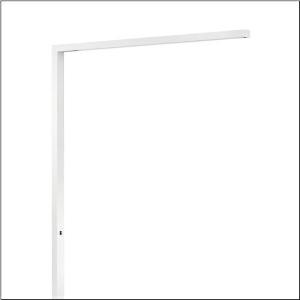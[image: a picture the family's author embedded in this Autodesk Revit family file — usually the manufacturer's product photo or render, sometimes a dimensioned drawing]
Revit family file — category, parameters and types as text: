
# Revit family: silica_r__11_floor_5mx51bs3wzk00002xx_06fb
name_source: partatom
category: Lighting Fixtures
units: mm (PartAtom-declared; Revit-internal decimal feet)

## family parameters
Cut with Voids When Loaded = No
Host = Face
Light Source = No
Part Type = Normal
Room Calculation Point = No
Round Connector Dimension = Use Diameter
Shared = No

## types (1)
- --- (1 x LED, 3960 lm / 8500 lm, 24.4 W / 54.9 W, 4000K)
    Apparent Load = 79 VA
    CIE Flux Codes = 82 97 100 100 100 / - - - 0 100
    Color Rendering = 80
    Color Temperature = 4000K
    Default Elevation = 1800 mm
    Description = Silica® 11 Floor, floorstanding luminaire, of PMMA, primary optical cover: cover panel, of PMMA, light emission: indirect/direct distribution, primary light characteristic: symmetric, installation type: not mounted, LED, rated luminous flux: 12.460lm, luminous efficacy: 157lm/W, light colour: 840, colour temperature: 4000K, daylight-dependent control, mains connection: 230V, AC, 50Hz, connection cable pre-assembled, cable length: 3m, rated input power: 79W, luminaire head, rectangular, rounded, of aluminium, coated, traffic white (RAL 9016), supporting column, angular, of aluminium, coated, traffic white (RAL 9016), baseplate, of steel, coated, traffic white (RAL 9016), length: 1.316mm, width: 65mm, protection rating (complete): IP20, insulation class (complete): insulation class I (protective earthing), certification: CE, permissible operating ambient temperature: 0..+35°C, standard: EN 50419, packaging unit: 1 piece
    Height = 40 mm  [stored 0.131234 ft]
    Lamp = 1 x LED
    Lamp Light Flux = 3960 lm / 8500 lm
    Lamp Power = 24.4 W / 54.9 W
    Lamp count = 1
    Length = 1317 mm
    Luminous efficacy = 157 lm/W
    Manufacturer = Siteco
    ModVariant = No
    Model = 5MX51BS3WZK00002XX
    Mounting Place = Floor
    Mounting Type = Freestanding
    Number of Poles = 1
    OnlyDefault = Yes
    Power Factor = 1
    Product Name = Silica® 11 Floor
    Product group = floorstanding luminaire
    ProductGroupID = 1301
    Protection Class = Protection class I
    Protection Degree = IP 20
    RLX_Detail_Level = 1
    RLX_Emergency_Light_Flux = 0 lm
    RLX_Emergency_Type = 0
    RLX_Emergency_Type_DB = No
    RlxData = <blob elided: 18153 chars, md5=e39972d7>
    Socket = socket
    Standby Power = 0 W
    System Light Flux = 12460 lm
    System Power = 79 W
    Type Comments = factory setting: direct and indirect light
    Type Image = l_1004655.jpg
    URL = http://relux.com
    VarID = @adj_155034
    Voltage = 0 V
    Weight = 0.00 kg
    Width = 65 mm

note: [stored X ft] marks values corroborated as IEEE doubles in the binary element streams (Revit-internal decimal feet)

## geometry (parser evidence)
native form markers: Blend x4, Sweep x13
no freeform markers — native parametric forms only
